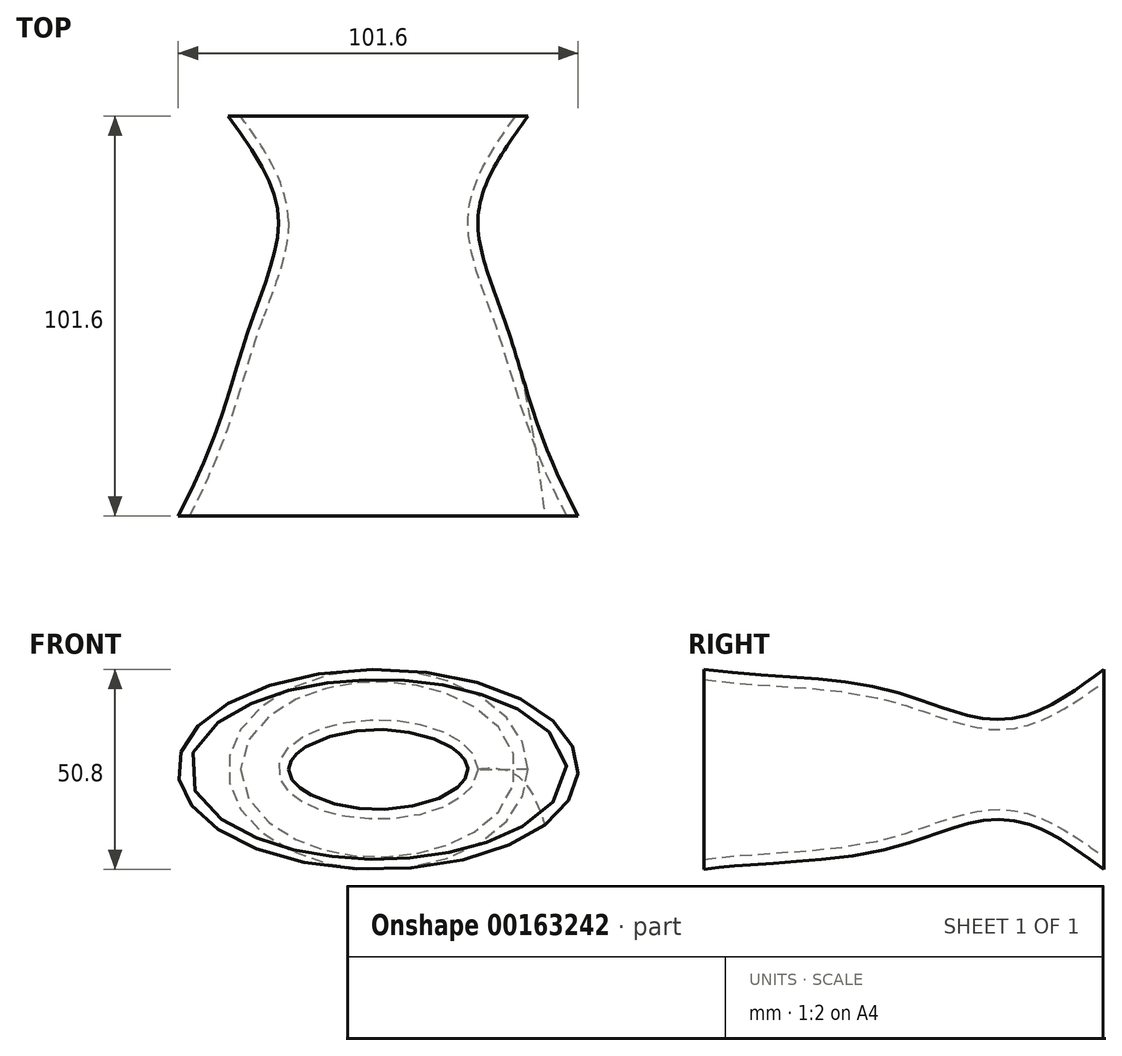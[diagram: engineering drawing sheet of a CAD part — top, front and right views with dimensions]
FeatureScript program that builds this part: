
annotation { "Feature Type Name" : "Feature", "Feature Type Description" : "" }
export const myFeature = defineFeature(function(context is Context, id is Id, definition is map)
    precondition{}
    {
        {
            var Q0;
            Q0=qCreatedBy(makeId("Front.planeOp"),FACE);
            cPlane(context, id + "F0", {"entities" : qUnion([Q0]), "cplaneType" : CPlaneType.OFFSET, "offset" : 25.4 * mm, "width" : 152.4 * mm, "height" : 152.4 * mm});
        }
        {
            var Q0;
            Q0=qCreatedBy(id+"F0.planeOp",FACE);
            cPlane(context, id + "F1", {"entities" : qUnion([Q0]), "cplaneType" : CPlaneType.OFFSET, "offset" : 25.4 * mm, "width" : 152.4 * mm, "height" : 152.4 * mm});
        }
        {
            var Q0;
            Q0=qCreatedBy(id+"F1.planeOp",FACE);
            cPlane(context, id + "F2", {"entities" : qUnion([Q0]), "cplaneType" : CPlaneType.OFFSET, "offset" : 50.8 * mm, "width" : 152.4 * mm, "height" : 152.4 * mm});
        }
        {
            var Q0;
            Q0=qCreatedBy(makeId("Front.planeOp"),FACE);
            var sketch = newSketch(context, id + "F3", { "sketchPlane" : qUnion([Q0])});
            skEllipse(sketch, "E0", {"center": v(0, 0) * mm, "majorRadius": 38.1 * mm, "minorRadius": 25.4 * mm, "majorAxis": v(1, 0)});
            skSolve(sketch);
        }
        {
            var Q0;
            Q0=qCreatedBy(id+"F0.planeOp",FACE);
            var sketch = newSketch(context, id + "F4", { "sketchPlane" : qUnion([Q0])});
            skEllipse(sketch, "E1", {"center": v(0, 0) * mm, "majorRadius": 25.4 * mm, "minorRadius": 12.7 * mm, "majorAxis": v(1, 0)});
            skSolve(sketch);
        }
        {
            var Q0;
            Q0=qCreatedBy(id+"F1.planeOp",FACE);
            var sketch = newSketch(context, id + "F5", { "sketchPlane" : qUnion([Q0])});
            skEllipse(sketch, "E2", {"center": v(0, 0) * mm, "majorRadius": 31.75 * mm, "minorRadius": 19.05 * mm, "majorAxis": v(1, 0)});
            skSolve(sketch);
        }
        {
            var Q0;
            Q0=qCreatedBy(id+"F2.planeOp",FACE);
            var sketch = newSketch(context, id + "F6", { "sketchPlane" : qUnion([Q0])});
            skEllipse(sketch, "E3", {"center": v(0, 0) * mm, "majorRadius": 50.8 * mm, "minorRadius": 25.4 * mm, "majorAxis": v(1, 0)});
            skSolve(sketch);
        }
        {
            var Q0;
            Q0=makeQuery(id+"F3.imprint","IMPRINT",FACE,{"disambiguationData":[TD([[makeQuery(id+"F3.imprint","IMPRINT",EDGE,{"derivedFrom":sQuery(id+"F3.wireOp",EDGE,"E0")}),1.0]])]});
            var Q1;
            Q1=makeQuery(id+"F4.imprint","IMPRINT",FACE,{"disambiguationData":[TD([[makeQuery(id+"F4.imprint","IMPRINT",EDGE,{"derivedFrom":sQuery(id+"F4.wireOp",EDGE,"E1")}),1.0]])]});
            var Q2;
            Q2=makeQuery(id+"F5.imprint","IMPRINT",FACE,{"disambiguationData":[TD([[makeQuery(id+"F5.imprint","IMPRINT",EDGE,{"derivedFrom":sQuery(id+"F5.wireOp",EDGE,"E2")}),1.0]])]});
            var Q3;
            Q3=makeQuery(id+"F6.imprint","IMPRINT",FACE,{"disambiguationData":[TD([[makeQuery(id+"F6.imprint","IMPRINT",EDGE,{"derivedFrom":sQuery(id+"F6.wireOp",EDGE,"E3")}),1.0]])]});
            loft(context, id + "F7", {"sheetProfilesArray" : [{ "sheetProfileEntities" : qUnion([Q0]) }, { "sheetProfileEntities" : qUnion([Q1]) }, { "sheetProfileEntities" : qUnion([Q2]) }, { "sheetProfileEntities" : qUnion([Q3]) }]});
        }
        {
            var Q0;
            Q0=makeQuery(id+"F7.opLoft","CAP_FACE",FACE,{"disambiguationData":[OSD([makeQuery(id+"F6.imprint","IMPRINT",FACE,{"disambiguationData":[TD([[makeQuery(id+"F6.imprint","IMPRINT",EDGE,{"derivedFrom":sQuery(id+"F6.wireOp",EDGE,"E3")}),1.0]])]})])],"isStart":true});
            var Q1;
            Q1=makeQuery(id+"F7.opLoft","CAP_FACE",FACE,{"disambiguationData":[OSD([makeQuery(id+"F3.imprint","IMPRINT",FACE,{"disambiguationData":[TD([[makeQuery(id+"F3.imprint","IMPRINT",EDGE,{"derivedFrom":sQuery(id+"F3.wireOp",EDGE,"E0")}),1.0]])]})])],"isStart":true});
            shell(context, id + "F8", {"entities" : qUnion([Q0, Q1]), "thickness" : 2.54 * mm});
        }
    });
